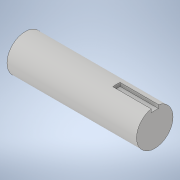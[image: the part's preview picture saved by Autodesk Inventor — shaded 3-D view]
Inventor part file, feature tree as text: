
AUTODESK INVENTOR PART (.ipt)
format: ipt  version: 2021 (Build 250183000, 183)  size: 109,056 bytes
history: native  units: in
note: dims shown in document units (in); Inventor stores cm internally (conversion verified against a paired STEP export)
features: extrude x2, sketch x2, plane x1
ambient origin geometry x8: Origin, YZ Plane, XZ Plane, XY Plane, X Axis, Y Axis, Z Axis, Center Point
bodies: Solid1 (feature_tree)
feature tree (5):
  extrude  "Extrusion1"  Depth=4.44in TaperAngle=0.0deg
  plane  "Work Plane1"
  extrude  "Extrusion9"  Depth=0.25in
  sketch  "Sketch1"  dims[d0=1.25in d1=4.44in d2=0.0in]
  sketch  "Sketch9"  dims[d11=-2.0535in d26=0.25in d27=0.125in d28=1.313in d29=0.0in]
